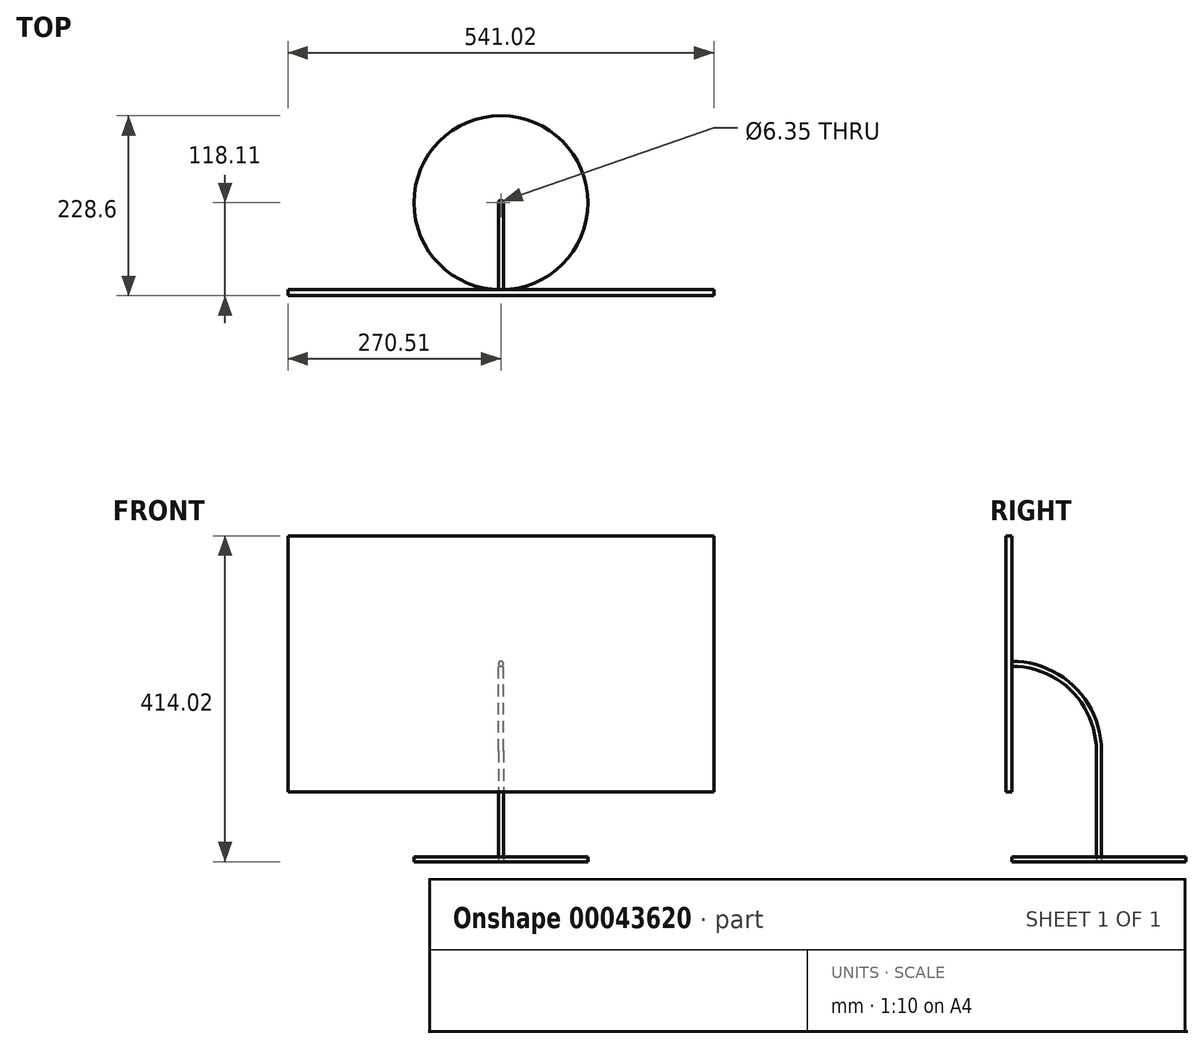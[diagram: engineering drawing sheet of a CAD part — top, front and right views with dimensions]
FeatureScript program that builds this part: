
annotation { "Feature Type Name" : "Feature", "Feature Type Description" : "" }
export const myFeature = defineFeature(function(context is Context, id is Id, definition is map)
    precondition{}
    {
        {
            var Q0;
            Q0=qCreatedBy(makeId("Front.planeOp"),FACE);
            var sketch = newSketch(context, id + "F0", { "sketchPlane" : qUnion([Q0])});
            skLineSegment(sketch, "E0.bottom", {"start": v(-270.51, 162.56) * mm, "end": v(270.51, 162.56) * mm});
            skLineSegment(sketch, "E0.top", {"start": v(-270.51, -162.56) * mm, "end": v(270.51, -162.56) * mm});
            skLineSegment(sketch, "E0.left", {"start": v(-270.51, 162.56) * mm, "end": v(-270.51, -162.56) * mm});
            skLineSegment(sketch, "E0.right", {"start": v(270.51, 162.56) * mm, "end": v(270.51, -162.56) * mm});
            skSolve(sketch);
        }
        {
            var Q0;
            Q0=makeQuery(id+"F0.imprint","IMPRINT",FACE,{"disambiguationData":[TD([[makeQuery(id+"F0.imprint","IMPRINT",EDGE,{"derivedFrom":sQuery(id+"F0.wireOp",EDGE,"E0.bottom")}),-1.0]])]});
            extrude(context, id + "F1", {"entities" : qUnion([Q0]), "depth" : 7.62 * mm});
        }
        {
            var Q0;
            Q0=qCreatedBy(makeId("Right.planeOp"),FACE);
            var sketch = newSketch(context, id + "F2", { "sketchPlane" : qUnion([Q0])});
            skArc(sketch, "E1", {"start": v(110.5, -110.49) * mm, "mid": v(78.13, -32.36) * mm, "end": v(0, 0) * mm});
            skLineSegment(sketch, "E2", {"start": v(110.5, -110.49) * mm, "end": v(110.5, -251.46) * mm});
            skSolve(sketch);
        }
        {
            var Q0;
            Q0=makeQuery(id+"F1.opExtrude","CAP_FACE",FACE,{"disambiguationData":[OSD([sQuery(id+"F0.wireOp",EDGE,"E0.bottom"),sQuery(id+"F0.wireOp",EDGE,"E0.top"),sQuery(id+"F0.wireOp",EDGE,"E0.left"),sQuery(id+"F0.wireOp",EDGE,"E0.right")])],"isStart":true});
            var sketch = newSketch(context, id + "F3", { "sketchPlane" : qUnion([Q0])});
            skCircle(sketch, "E3", {"center": v(0, 0) * mm, "radius": 3.17 * mm});
            skSolve(sketch);
        }
        {
            var Q0;
            Q0 = qSketchRegion(id + "F3", true);
            var Q1;
            Q1 = qConstructionFilter(qBodyType(qCreatedBy(id + "F2" ,EDGE), BodyType.WIRE), ConstructionObject.NO);
            sweep(context, id + "F4", {"operationType" : NewBodyOperationType.ADD, "profiles" : qUnion([Q0]), "path" : qUnion([Q1])});
        }
        {
            var Q0;
            Q0=makeQuery(id+"F4.opSweep","CAP_FACE",FACE,{"disambiguationData":[OSD([sQuery(id+"F2.wireOp",VERTEX,"E2.end"),sQuery(id+"F3.wireOp",EDGE,"E3")])],"isStart":false});
            var sketch = newSketch(context, id + "F5", { "sketchPlane" : qUnion([Q0])});
            skCircle(sketch, "E4", {"center": v(0, -110.49) * mm, "radius": 110.5 * mm});
            skSolve(sketch);
        }
        {
            var Q0;
            Q0=makeQuery(id+"F5.imprint","IMPRINT",FACE,{"disambiguationData":[TD([[makeQuery(id+"F5.imprint","IMPRINT",EDGE,{"derivedFrom":sQuery(id+"F5.wireOp",EDGE,"E4")}),1.0]])]});
            extrude(context, id + "F6", {"entities" : qUnion([Q0]), "oppositeDirection" : true, "depth" : 6.35 * mm});
        }
    });
